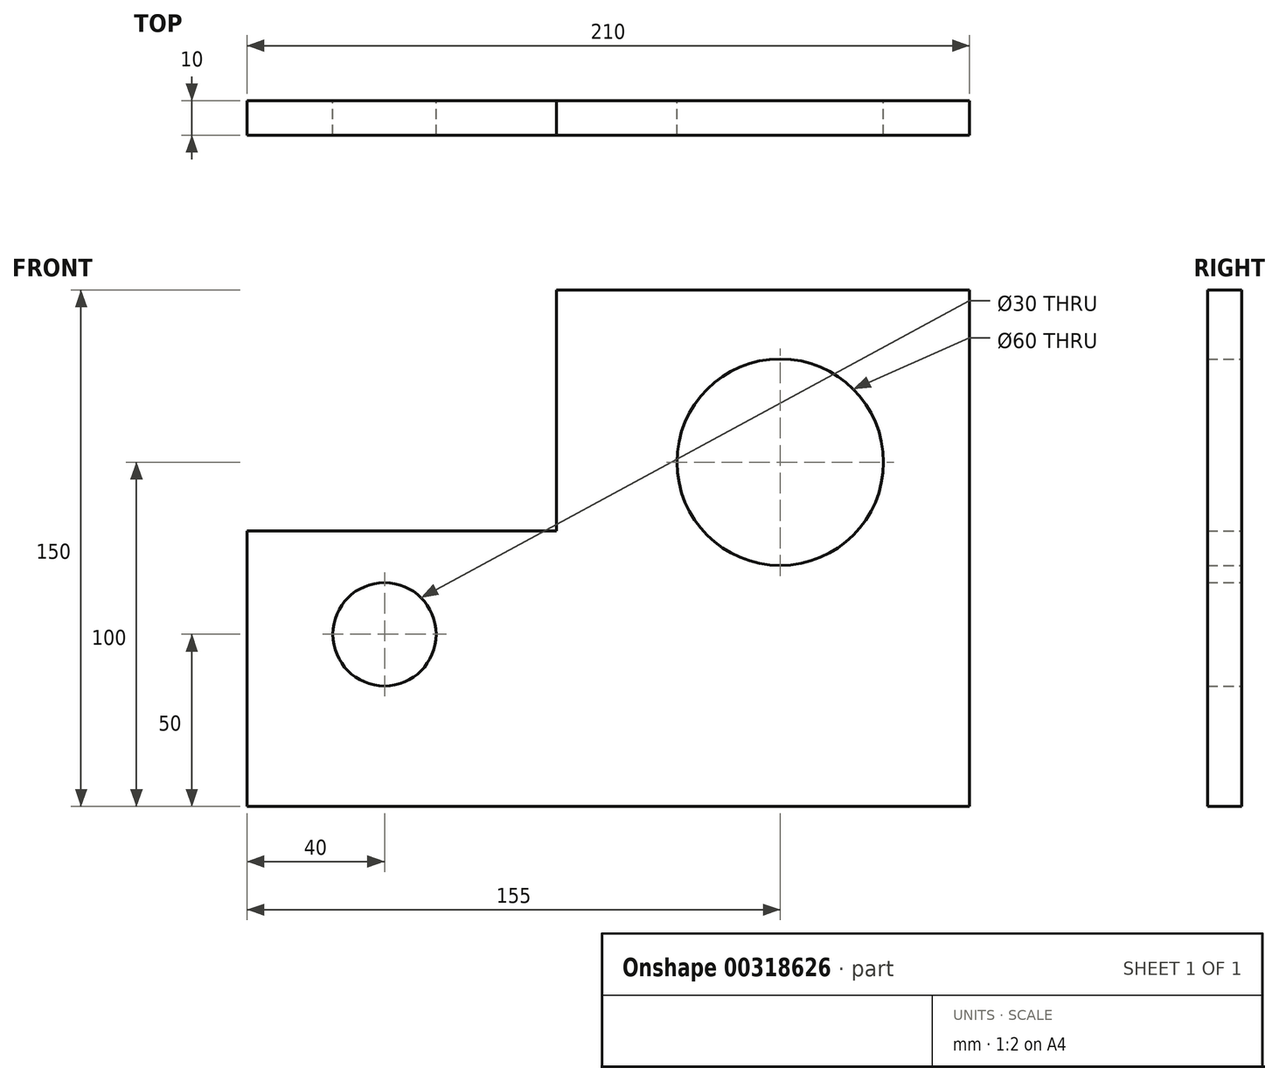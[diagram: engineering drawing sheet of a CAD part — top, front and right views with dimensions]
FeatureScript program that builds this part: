
annotation { "Feature Type Name" : "Feature", "Feature Type Description" : "" }
export const myFeature = defineFeature(function(context is Context, id is Id, definition is map)
    precondition{}
    {
        {
            var Q0;
            Q0=qCreatedBy(makeId("Front.planeOp"),FACE);
            var sketch = newSketch(context, id + "F0", { "sketchPlane" : qUnion([Q0])});
            skLineSegment(sketch, "E0", {"start": v(0, 0) * mm, "end": v(-210, 0) * mm});
            skLineSegment(sketch, "E1", {"start": v(-210, 0) * mm, "end": v(-210, 80) * mm});
            skLineSegment(sketch, "E2", {"start": v(-210, 80) * mm, "end": v(-120, 80) * mm});
            skLineSegment(sketch, "E3", {"start": v(-120, 80) * mm, "end": v(-120, 150) * mm});
            skLineSegment(sketch, "E4", {"start": v(-120, 150) * mm, "end": v(0, 150) * mm});
            skLineSegment(sketch, "E5", {"start": v(0, 150) * mm, "end": v(0, 0) * mm});
            skCircle(sketch, "E6", {"center": v(-170, 50) * mm, "radius": 15 * mm});
            skCircle(sketch, "E7", {"center": v(-55, 100) * mm, "radius": 30 * mm});
            skSolve(sketch);
        }
        {
            var Q0;
            Q0=makeQuery(id+"F0.imprint","IMPRINT",FACE,{"disambiguationData":[TD([[makeQuery(id+"F0.imprint","IMPRINT",EDGE,{"derivedFrom":sQuery(id+"F0.wireOp",EDGE,"E0")}),-1.0]])]});
            extrude(context, id + "F1", {"entities" : qUnion([Q0]), "depth" : 10 * mm});
        }
    });
